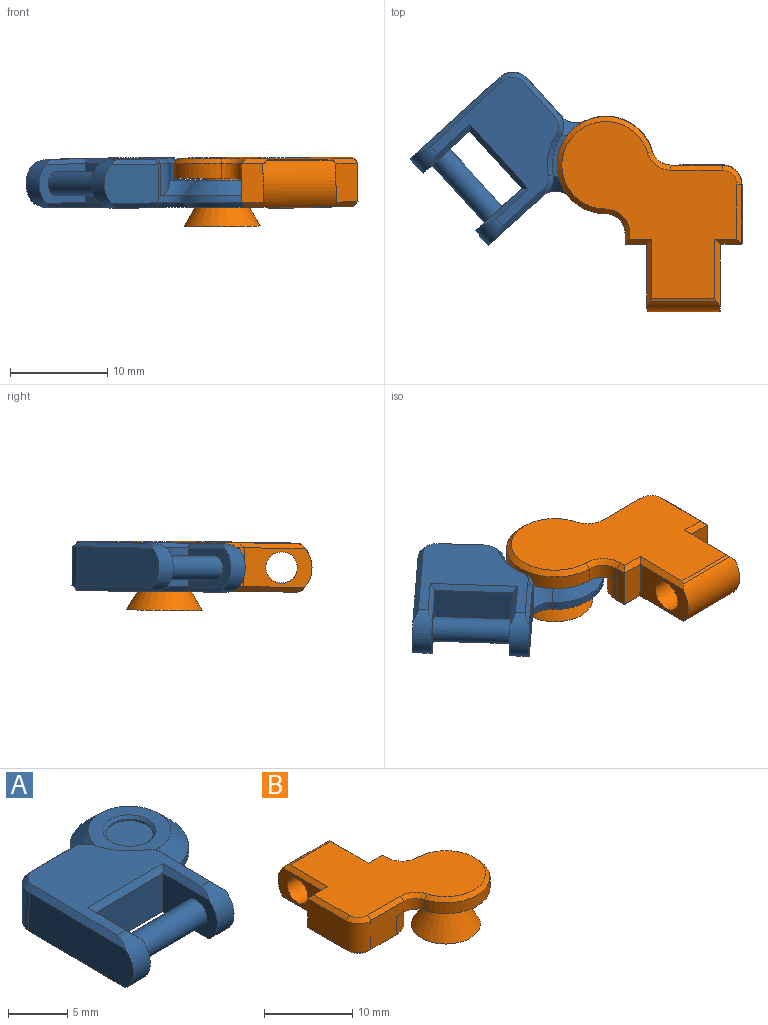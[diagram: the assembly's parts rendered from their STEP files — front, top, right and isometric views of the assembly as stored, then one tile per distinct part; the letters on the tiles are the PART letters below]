
ASSEMBLY  parts=2 mates=1
PART A: 48 faces, bbox 19.1x19.6x5.3 mm
  f0: plane 7.53x4.09mm, normal (1,0,0.01), area 28.8mm2, adj f6,f13,f14,f40
  f1: plane 6.53x4.08mm, normal (-1,0,-0.01), area 19.9mm2, adj f5,f12,f17,f40,f42
  f2: plane 6.53x4.08mm, normal (1,0,0.01), area 19.9mm2, adj f7,f11,f17,f41,f42
  f3: plane 12.53x4.16mm, normal (-1,0,-0.01), area 48.8mm2, adj f8,f10,f18,f41
  f4: plane 18x16.53mm, normal (0.01,0.01,-1), area 106.5mm2, adj f5,f6,f7,f8,f26,f27,f28,f29
  f5: plane 6.01x0.55mm, normal (-0.7,0.01,-0.71), area 3.7mm2, adj f1,f4,f27,f40
  f6: plane 6.51x0.57mm, normal (0.71,0.01,-0.7), area 4.3mm2, adj f0,f4,f28,f40
  f7: plane 6.01x0.56mm, normal (0.71,0.01,-0.7), area 3.7mm2, adj f2,f4,f27,f41
  f8: plane 11.51x0.64mm, normal (-0.7,0.01,-0.71), area 7.8mm2, adj f3,f4,f32,f41
  f9: plane 11.53x11.05mm, normal (-0.01,-0.01,1), area 73.3mm2, adj f10,f11,f12,f13,f33,f34,f35,f36
  f10: plane 11.5x0.66mm, normal (-0.71,-0.01,0.7), area 7.8mm2, adj f3,f9,f33,f41
  f11: plane 5.99x0.58mm, normal (0.7,-0.01,0.71), area 3.7mm2, adj f2,f9,f34,f41
  f12: plane 5.99x0.59mm, normal (-0.71,-0.01,0.7), area 3.7mm2, adj f1,f9,f34,f40
  f13: plane 6.5x0.59mm, normal (0.7,-0.01,0.71), area 4.3mm2, adj f0,f9,f39,f40
  f14: cylinder r=2mm len=4.04mm, axis (-0.01,-0.01,1), area 3.4mm2, adj f0,f16,f24,f28,f39,f43
  f15: cylinder r=2mm len=1.92mm, axis (-0.01,-0.01,1), area 1.9mm2, adj f16,f19,f30,f45
  f16: cylinder r=5mm len=10.01mm, axis (-0.01,-0.01,1), area 16.6mm2, adj f14,f15,f29,f44
  f17: plane 8.03x4.06mm, normal (0,-1,-0.01), area 32mm2, adj f1,f2,f27,f34
  f18: cylinder r=2mm len=4.04mm, axis (-0.01,-0.01,1), area 12.6mm2, adj f3,f19,f32,f33
  f19: plane 5.32x4.04mm, normal (0,1,0.01), area 19.5mm2, adj f15,f18,f23,f31,f35,f46
  f20: cylinder r=5.5mm len=3.23mm, axis (-0.01,-0.01,1), area 7.2mm2, adj f21,f23,f24,f37
  f21: plane 8.88x8.3mm, normal (-0.01,-0.01,1), area 31.9mm2, adj f20,f23,f24,f43,f44,f45,f47
  f22: cone r=1.75mm half-angle=30deg, axis (0.01,0.01,-1), area 38.9mm2, adj f25,f26
  f23: cylinder r=2mm len=3.26mm, axis (-0.01,-0.01,1), area 6.8mm2, adj f19,f20,f21,f36,f45,f46
  f24: cylinder r=2mm len=3.27mm, axis (-0.01,-0.01,1), area 6.1mm2, adj f14,f20,f21,f38,f43
  f25: cylinder r=2mm len=4mm, axis (-0.01,-0.01,1), area 2.3mm2, adj f22,f47
  f26: cone r=3.19mm half-angle=60deg, axis (0.01,0.01,-1), area 10.7mm2, adj f4,f22
  f27: plane 9x0.56mm, normal (0.01,-0.7,-0.72), area 6mm2, adj f4,f5,f7,f17
  f28: cone r=2mm half-angle=45deg, axis (0.01,0.01,-1), area 2.5mm2, adj f4,f6,f14,f29
  f29: cone r=4.5mm half-angle=45deg, axis (-0.01,-0.01,1), area 14.9mm2, adj f4,f16,f28,f30
  f30: cone r=2mm half-angle=45deg, axis (0.01,0.01,-1), area 2mm2, adj f4,f15,f29,f31
  f31: plane 5.3x0.55mm, normal (0.01,0.72,-0.7), area 3.7mm2, adj f4,f19,f30,f32
  f32: cone r=1.5mm half-angle=45deg, axis (-0.01,-0.01,1), area 1.9mm2, adj f4,f8,f18,f31
  f33: cone r=2mm half-angle=45deg, axis (0.01,0.01,-1), area 1.9mm2, adj f9,f10,f18,f35
  f34: plane 9x0.58mm, normal (-0.01,-0.72,0.7), area 6mm2, adj f9,f11,f12,f17
  f35: plane 4.78x0.53mm, normal (-0.01,0.7,0.72), area 3.4mm2, adj f9,f19,f33,f36
  f36: cone r=1.5mm half-angle=45deg, axis (0.01,0.01,-1), area 1.6mm2, adj f9,f23,f35,f37
  f37: cone r=6mm half-angle=45deg, axis (-0.01,-0.01,1), area 3mm2, adj f9,f20,f36,f38
  f38: cone r=1.5mm half-angle=45deg, axis (0.01,0.01,-1), area 1.5mm2, adj f9,f24,f37,f39
  f39: cone r=2.5mm half-angle=45deg, axis (-0.01,-0.01,1), area 0.2mm2, adj f9,f13,f14,f38
  f40: cylinder r=2.5mm len=5.02mm, axis (-1,0,-0.01), area 13.5mm2, adj f0,f1,f4,f5,f6,f9,f12,f13
  f41: cylinder r=2.5mm len=5.02mm, axis (-1,0,-0.01), area 13.5mm2, adj f2,f3,f4,f7,f8,f9,f10,f11
  f42: cylinder r=1.25mm len=8.02mm, axis (-1,0,-0.01), area 62.8mm2, adj f1,f2
  f43: cone r=3.5mm half-angle=45deg, axis (-0.01,-0.01,1), area 5.6mm2, adj f14,f21,f24,f44
  f44: cone r=5mm half-angle=45deg, axis (0.01,0.01,-1), area 39.9mm2, adj f16,f21,f43,f45
  f45: cone r=3.5mm half-angle=45deg, axis (-0.01,-0.01,1), area 5.7mm2, adj f15,f21,f23,f44,f46
  f46: plane 0.55x0.11mm, normal (-0.01,0.7,0.72), area 0mm2, adj f19,f23,f45
  f47: cone r=2mm half-angle=45deg, axis (-0.01,-0.01,1), area 4.7mm2, adj f21,f25
PART B: 47 faces, bbox 19x20.1x7 mm
  f0: plane 7x4mm, normal (1,0,0), area 18.8mm2, adj f6,f20,f21,f30,f43
  f1: plane 7x4mm, normal (-1,0,0), area 18.8mm2, adj f7,f20,f21,f26,f39
  f2: cylinder r=1.75mm len=3.5mm, axis (0,0,-1), area 13.9mm2, adj f15,f16
  f3: cylinder r=2mm len=4mm, axis (0,0,-1), area 4.8mm2, adj f5,f12,f15,f19,f31,f44
  f4: plane 13.2x11mm, normal (0,0,-1), area 104.4mm2, adj f34,f35,f36,f37,f38,f39,f40,f41
  f5: plane 4x1.13mm, normal (1,0,0), area 4.5mm2, adj f3,f6,f33,f46
  f6: plane 4x2.25mm, normal (0,1,0), area 9mm2, adj f0,f5,f32,f45
  f7: plane 4x2.25mm, normal (0,1,0), area 9mm2, adj f1,f8,f24,f37
  f8: plane 6.13x4mm, normal (-1,0,0), area 24.5mm2, adj f7,f9,f22,f35
  f9: cylinder r=2mm len=4mm, axis (0,0,-1), area 12.6mm2, adj f8,f10,f23,f34
  f10: plane 5.29x4mm, normal (0,-1,0), area 18.1mm2, adj f9,f11,f15,f18,f25,f36
  f11: cylinder r=2mm len=1.92mm, axis (0,0,-1), area 3.8mm2, adj f10,f12,f15,f27
  f12: cylinder r=5mm len=10mm, axis (0,0,-1), area 33.2mm2, adj f3,f11,f15,f29
  f13: plane 18.2x18mm, normal (0,0,1), area 179.6mm2, adj f22,f23,f24,f25,f26,f27,f28,f29
  f14: cylinder r=5.5mm len=2.51mm, axis (0,0,-1), area 8mm2, adj f15,f18,f19,f40
  f15: plane 12.95x11.95mm, normal (0,0,-1), area 75.1mm2, adj f2,f3,f10,f11,f12,f14,f18,f19
  f16: cone r=2.75mm half-angle=30deg, axis (0,0,-1), area 76.6mm2, adj f2,f17
  f17: plane 7.81x7.81mm, normal (0,0,-1), area 47.9mm2, adj f16
  f18: cylinder r=3mm len=2.81mm, axis (0,0,-1), area 9.1mm2, adj f10,f14,f15,f38
  f19: cylinder r=3mm len=2.5mm, axis (0,0,-1), area 7.3mm2, adj f3,f14,f15,f42
  f20: cylinder r=3.12mm len=7.5mm, axis (1,0,0), area 40.2mm2, adj f0,f1,f26,f28,f30,f39,f41,f43
  f21: cylinder r=1.62mm len=7.5mm, axis (1,0,0), area 76.6mm2, adj f0,f1
  f22: plane 6.13x0.5mm, normal (-0.71,0,0.71), area 4.2mm2, adj f8,f13,f23,f24
  f23: cone r=1.5mm half-angle=45deg, axis (0,0,-1), area 1.9mm2, adj f9,f13,f22,f25
  f24: plane 2.75x0.5mm, normal (0,0.71,0.71), area 1.6mm2, adj f7,f13,f22,f26
  f25: plane 5.29x0.5mm, normal (0,-0.71,0.71), area 3.7mm2, adj f10,f13,f23,f27
  f26: plane 6.79x0.52mm, normal (-0.71,0,0.71), area 4.4mm2, adj f1,f13,f20,f24,f28
  f27: cone r=2mm half-angle=45deg, axis (0,0,1), area 2mm2, adj f11,f13,f25,f29
  f28: plane 6.74x0.32mm, normal (0,0.35,0.94), area 2.3mm2, adj f13,f20,f26,f30
  f29: cone r=4.5mm half-angle=45deg, axis (0,0,-1), area 14.9mm2, adj f12,f13,f27,f31
  f30: plane 6.79x0.52mm, normal (0.71,0,0.71), area 4.4mm2, adj f0,f13,f20,f28,f32
  f31: cone r=2mm half-angle=45deg, axis (0,0,1), area 2.5mm2, adj f3,f13,f29,f33
  f32: plane 2.75x0.5mm, normal (0,0.71,0.71), area 1.6mm2, adj f6,f13,f30,f33
  f33: plane 1.13x0.5mm, normal (0.71,0,0.71), area 0.6mm2, adj f5,f13,f31,f32
  f34: cone r=2mm half-angle=45deg, axis (0,0,1), area 1.9mm2, adj f4,f9,f35,f36
  f35: plane 6.13x0.5mm, normal (-0.71,0,-0.71), area 4.2mm2, adj f4,f8,f34,f37
  f36: plane 4.05x0.5mm, normal (0,-0.71,-0.71), area 2.9mm2, adj f4,f10,f34,f38
  f37: plane 2.75x0.5mm, normal (0,0.71,-0.71), area 1.6mm2, adj f4,f7,f35,f39
  f38: cone r=2.5mm half-angle=45deg, axis (0,0,1), area 2.4mm2, adj f4,f18,f36,f40
  f39: plane 6.79x0.52mm, normal (-0.71,0,-0.71), area 4.4mm2, adj f1,f4,f20,f37,f41
  f40: cone r=6mm half-angle=45deg, axis (0,0,-1), area 2.4mm2, adj f4,f14,f38,f42
  f41: plane 6.74x0.32mm, normal (0,0.35,-0.94), area 2.3mm2, adj f4,f20,f39,f43
  f42: cone r=2.5mm half-angle=45deg, axis (0,0,1), area 1.9mm2, adj f4,f19,f40,f44
  f43: plane 6.79x0.52mm, normal (0.71,0,-0.71), area 4.4mm2, adj f0,f4,f20,f41,f45
  f44: cone r=2.5mm half-angle=45deg, axis (0,0,-1), area 0mm2, adj f3,f4,f42,f46
  f45: plane 2.75x0.5mm, normal (0,0.71,-0.71), area 1.6mm2, adj f4,f6,f43,f46
  f46: plane 1.13x0.5mm, normal (0.71,0,-0.71), area 0.6mm2, adj f4,f5,f44,f45
PLACE A rot(axis=(0.01,0.01,-1),47.8deg) t=(4.03,1.95,-15.89)mm
PLACE B rot(axis=(0,-0.01,1),180deg) t=(-1.67,37.97,-0.34)mm fixed
MATE revolute A.f16 <-> B.f2  axis (0.01,0.01,-1) through (7.9,7.57,-0.69)mm
